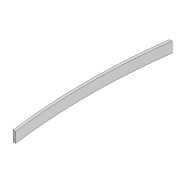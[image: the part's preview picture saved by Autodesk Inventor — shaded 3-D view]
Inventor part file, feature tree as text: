
AUTODESK INVENTOR PART (.ipt)
format: ipt  version: 2022 (Build 260153000, 153)  size: 78,336 bytes
history: native  units: mm
features: extrude x1, sketch x1
ambient origin geometry x8: Origin, YZ Plane, XZ Plane, XY Plane, X Axis, Y Axis, Z Axis, Center Point
bodies: Solid1 (feature_tree)
feature tree (2):
  extrude  "Extrusion1"  Depth=2.0mm
  sketch  "Sketch1"  dims[d0=30.0mm d1=1.0mm d2=2.0mm d3=0.0mm]
